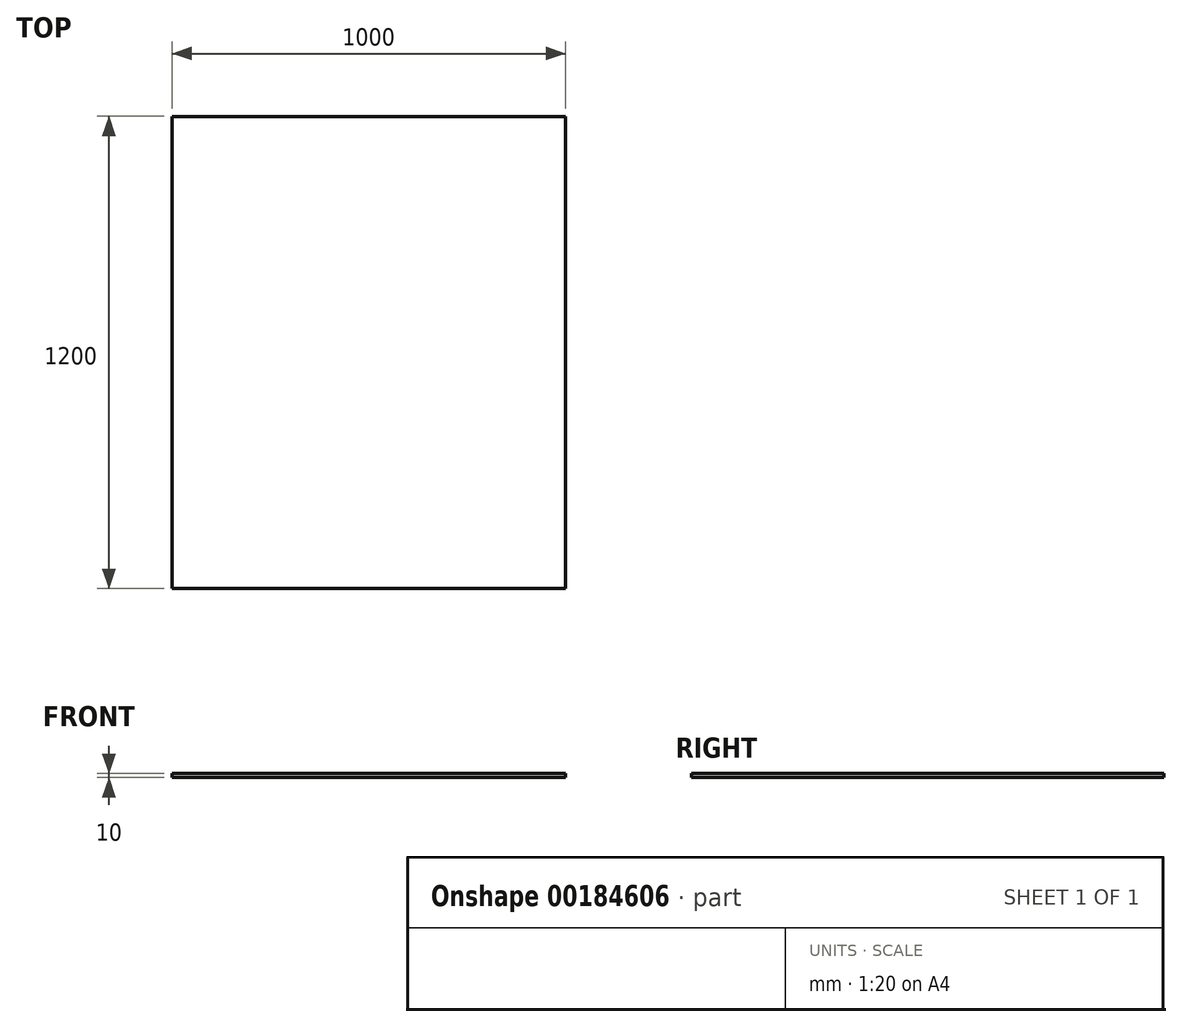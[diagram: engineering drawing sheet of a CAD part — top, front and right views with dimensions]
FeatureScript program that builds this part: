
annotation { "Feature Type Name" : "Feature", "Feature Type Description" : "" }
export const myFeature = defineFeature(function(context is Context, id is Id, definition is map)
    precondition{}
    {
        {
            var Q0;
            Q0=qCreatedBy(makeId("Top.planeOp"),FACE);
            var sketch = newSketch(context, id + "F0", { "sketchPlane" : qUnion([Q0])});
            skLineSegment(sketch, "E0.bottom", {"start": v(-497.4, 961.62) * mm, "end": v(502.6, 961.62) * mm});
            skLineSegment(sketch, "E0.top", {"start": v(-497.4, -238.38) * mm, "end": v(502.6, -238.38) * mm});
            skLineSegment(sketch, "E0.left", {"start": v(-497.4, 961.62) * mm, "end": v(-497.4, -238.38) * mm});
            skLineSegment(sketch, "E0.right", {"start": v(502.6, 961.62) * mm, "end": v(502.6, -238.38) * mm});
            skSolve(sketch);
        }
        {
            var Q0;
            Q0=makeQuery(id+"F0.imprint","IMPRINT",FACE,{"disambiguationData":[TD([[makeQuery(id+"F0.imprint","IMPRINT",EDGE,{"derivedFrom":sQuery(id+"F0.wireOp",EDGE,"E0.bottom")}),-1.0]])]});
            extrude(context, id + "F1", {"entities" : qUnion([Q0]), "depth" : 10 * mm});
        }
    });
